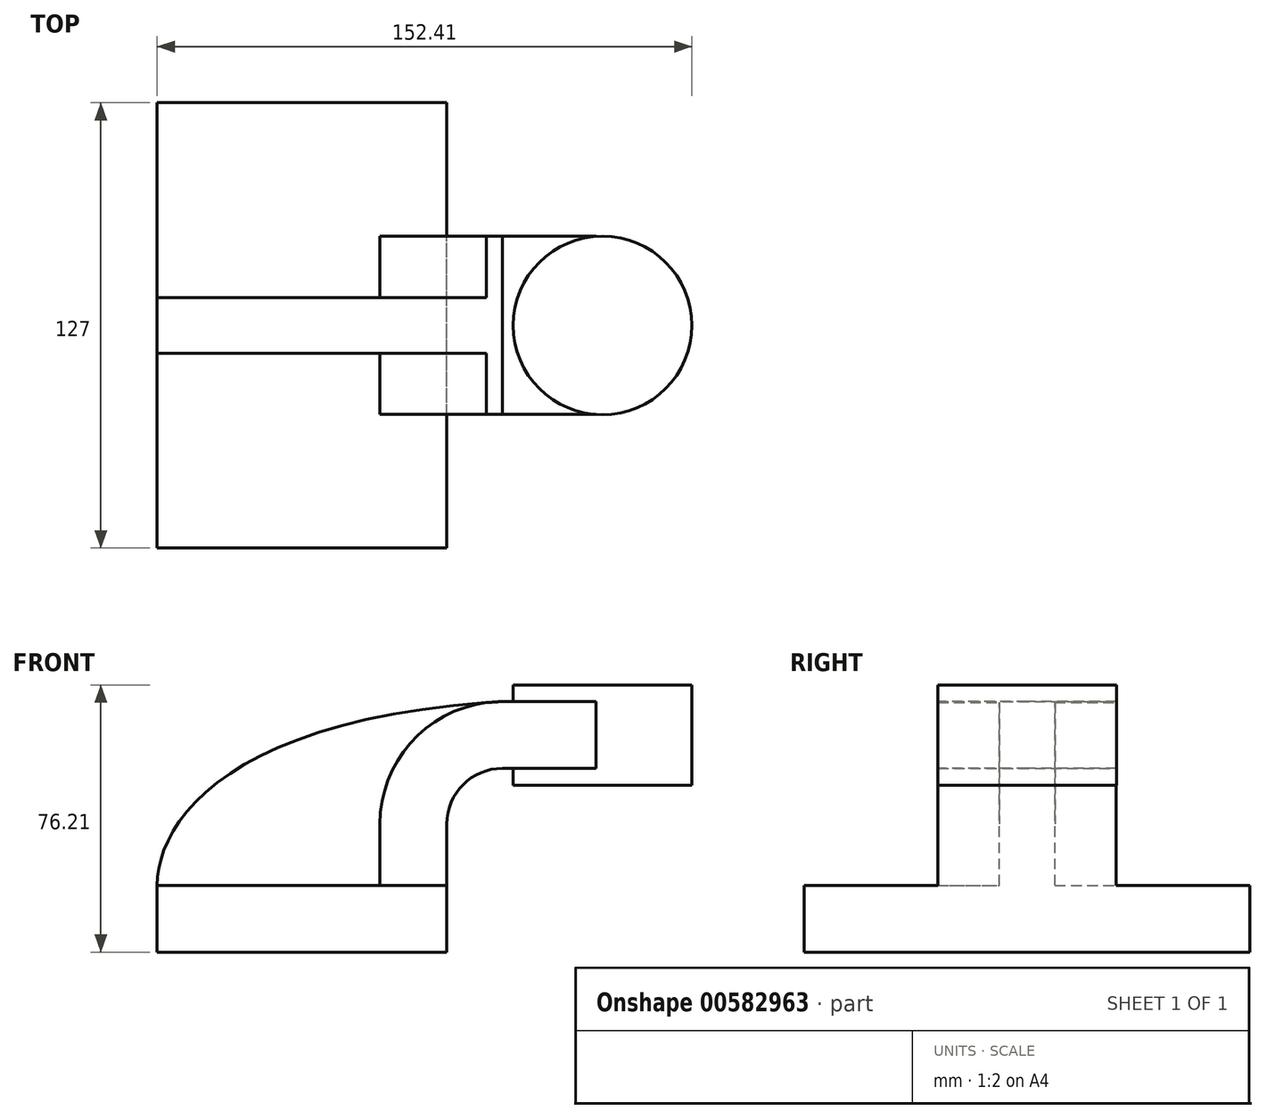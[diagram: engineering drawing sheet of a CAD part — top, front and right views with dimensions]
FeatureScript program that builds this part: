
annotation { "Feature Type Name" : "Feature", "Feature Type Description" : "" }
export const myFeature = defineFeature(function(context is Context, id is Id, definition is map)
    precondition{}
    {
        {
            var Q0;
            Q0=qCreatedBy(makeId("Front.planeOp"),FACE);
            var sketch = newSketch(context, id + "F0", { "sketchPlane" : qUnion([Q0])});
            skLineSegment(sketch, "E0.bottom", {"start": v(-41.28, -9.53) * mm, "end": v(41.28, -9.53) * mm});
            skLineSegment(sketch, "E0.top", {"start": v(-41.28, 9.53) * mm, "end": v(41.28, 9.53) * mm});
            skLineSegment(sketch, "E0.left", {"start": v(-41.28, -9.53) * mm, "end": v(-41.28, 9.53) * mm});
            skLineSegment(sketch, "E0.right", {"start": v(41.28, -9.53) * mm, "end": v(41.28, 9.53) * mm});
            skPoint(sketch, "E0.middle", {"position": v(0, 0) * mm});
            skLineSegment(sketch, "E1.bottom", {"start": v(60.33, 38.1) * mm, "end": v(111.12, 38.1) * mm});
            skLineSegment(sketch, "E1.top", {"start": v(60.33, 66.67) * mm, "end": v(111.12, 66.67) * mm});
            skLineSegment(sketch, "E1.left", {"start": v(60.33, 38.1) * mm, "end": v(60.33, 66.67) * mm});
            skLineSegment(sketch, "E1.right", {"start": v(111.12, 38.1) * mm, "end": v(111.12, 66.67) * mm});
            skPoint(sketch, "E1.middle", {"position": v(85.72, 52.39) * mm});
            skLineSegment(sketch, "E2", {"start": v(41.27, 9.52) * mm, "end": v(41.27, 27) * mm});
            skArc(sketch, "E3", {"start": v(41.27, 27) * mm, "mid": v(45.92, 38.23) * mm, "end": v(57.15, 42.88) * mm});
            skLineSegment(sketch, "E4", {"start": v(57.15, 42.88) * mm, "end": v(85.65, 42.88) * mm});
            skLineSegment(sketch, "E5.0", {"start": v(57.15, 61.93) * mm, "end": v(85.65, 61.93) * mm});
            skArc(sketch, "E5.1", {"start": v(22.22, 27) * mm, "mid": v(32.45, 51.7) * mm, "end": v(57.15, 61.93) * mm});
            skLineSegment(sketch, "E5.2", {"start": v(22.22, 9.52) * mm, "end": v(22.22, 27) * mm});
            skLineSegment(sketch, "E6", {"start": v(85.65, 38.1) * mm, "end": v(85.65, 66.67) * mm});
            skFitSpline(sketch, "E7", {"points": [v(-41.28, 9.53) * mm, v(57.15, 61.93) * mm], "startDerivative": vector(-0.08, 53.61) * mm, "endDerivative": vector(235.52, 13.84) * mm});
            skSolve(sketch);
        }
        {
            var Q0;
            Q0=makeQuery(id+"F0.imprint","IMPRINT",FACE,{"disambiguationData":[TD([[makeQuery(id+"F0.imprint","IMPRINT",EDGE,{"derivedFrom":sQuery(id+"F0.wireOp",EDGE,"E0.bottom")}),1.0]])]});
            extrude(context, id + "F1", {"entities" : qUnion([Q0]), "endBound" : BoundingType.SYMMETRIC, "depth" : 127 * mm, "offsetDistance" : 25.4 * mm});
        }
        {
            var Q0;
            {var subQ1=sQuery(id+"F0.wireOp",EDGE,"E2");Q0=makeQuery(id+"F0.imprint","IMPRINT",FACE,{"disambiguationData":[TD([[makeQuery(id+"F0.imprint","IMPRINT",EDGE,{"derivedFrom":subQ1}),1.0]])]});}
            var Q1;
            {var subQ0=sQuery(id+"F0.wireOp",EDGE,"E4");var subQ1=sQuery(id+"F0.wireOp",EDGE,"E1.left");var subQ2=makeQuery(id+"F0.imprint","INTERSECT",VERTEX,{"derivedFrom":[subQ1,subQ0]});Q1=makeQuery(id+"F0.imprint","IMPRINT",FACE,{"disambiguationData":[TD([[makeQuery(id+"F0.imprint","IMPRINT",EDGE,{"disambiguationData":[TD([[subQ2,-1.0]])],"derivedFrom":subQ1}),-1.0]])]});}
            extrude(context, id + "F2", {"entities" : qUnion([Q0, Q1]), "operationType" : NewBodyOperationType.ADD, "endBound" : BoundingType.SYMMETRIC, "depth" : 50.8 * mm, "offsetDistance" : 25.4 * mm});
        }
        {
            var Q0;
            {var subQ3=sQuery(id+"F0.wireOp",EDGE,"E5.2");Q0=makeQuery(id+"F0.imprint","IMPRINT",FACE,{"disambiguationData":[TD([[makeQuery(id+"F0.imprint","IMPRINT",EDGE,{"derivedFrom":subQ3}),1.0]])]});}
            extrude(context, id + "F3", {"entities" : qUnion([Q0]), "operationType" : NewBodyOperationType.ADD, "endBound" : BoundingType.SYMMETRIC, "depth" : 15.88 * mm, "offsetDistance" : 25.4 * mm});
        }
        {
            var Q0;
            {var subQ4=sQuery(id+"F0.wireOp",EDGE,"E1.right");Q0=makeQuery(id+"F0.imprint","IMPRINT",FACE,{"disambiguationData":[TD([[makeQuery(id+"F0.imprint","IMPRINT",EDGE,{"derivedFrom":subQ4}),1.0]])]});}
            var Q1;
            Q1=sQuery(id+"F0.wireOp",EDGE,"E6");
            revolve(context, id + "F4", {"operationType" : NewBodyOperationType.ADD, "entities" : qUnion([Q0]), "axis" : qUnion([Q1]), "revolveType" : RevolveType.FULL});
        }
    });
